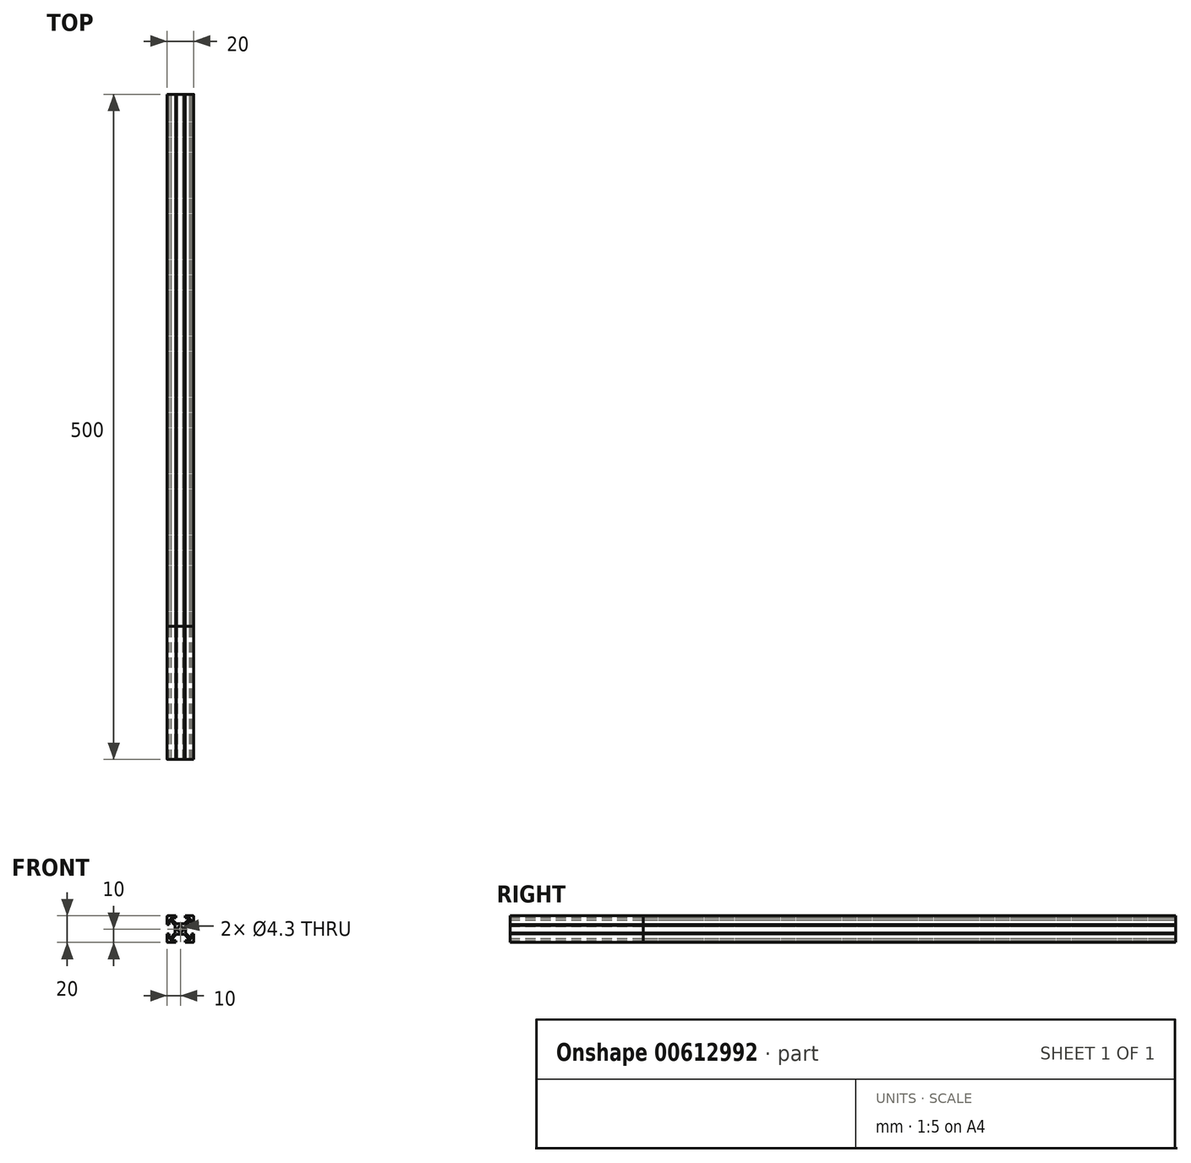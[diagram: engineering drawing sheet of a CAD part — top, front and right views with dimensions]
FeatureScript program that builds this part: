
annotation { "Feature Type Name" : "Feature", "Feature Type Description" : "" }
export const myFeature = defineFeature(function(context is Context, id is Id, definition is map)
    precondition{}
    {
        {
            var Q0;
            Q0=qCreatedBy(makeId("Front.planeOp"),FACE);
            var sketch = newSketch(context, id + "F0", { "sketchPlane" : qUnion([Q0])});
            skLineSegment(sketch, "E0", {"start": v(23.23, 0) * mm, "end": v(-24.5, 0) * mm, "construction": true});
            skLineSegment(sketch, "E1", {"start": v(0, 19.26) * mm, "end": v(0, -20.24) * mm, "construction": true});
            skLineSegment(sketch, "E2.bottom", {"start": v(4, 4) * mm, "end": v(-4, 4) * mm});
            skLineSegment(sketch, "E2.top", {"start": v(4, -4) * mm, "end": v(-4, -4) * mm});
            skLineSegment(sketch, "E2.left", {"start": v(4, 4) * mm, "end": v(4, -4) * mm});
            skLineSegment(sketch, "E2.right", {"start": v(-4, 4) * mm, "end": v(-4, -4) * mm});
            skPoint(sketch, "E2.middle", {"position": v(0, 0) * mm});
            skCircle(sketch, "E3", {"center": v(0, 0) * mm, "radius": 2.15 * mm});
            skLineSegment(sketch, "E4.right", {"start": v(10, 10) * mm, "end": v(10, -10) * mm, "construction": true});
            skLineSegment(sketch, "E5", {"start": v(-3.5, 10) * mm, "end": v(-9.67, 10) * mm});
            skLineSegment(sketch, "E6", {"start": v(-10, 9.67) * mm, "end": v(-10, 3.5) * mm});
            skLineSegment(sketch, "E7", {"start": v(-10, 3.5) * mm, "end": v(-8.5, 3.5) * mm});
            skLineSegment(sketch, "E8", {"start": v(-8.5, 3.5) * mm, "end": v(-8.5, 6.65) * mm});
            skLineSegment(sketch, "E9", {"start": v(-10, 10) * mm, "end": v(-4, 4) * mm, "construction": true});
            skLineSegment(sketch, "E10.trimOffspring", {"start": v(0, 10) * mm, "end": v(10, 10) * mm, "construction": true});
            skLineSegment(sketch, "E11", {"start": v(-3.5, 10) * mm, "end": v(-3.5, 8.5) * mm});
            skLineSegment(sketch, "E12", {"start": v(-3.5, 8.5) * mm, "end": v(-6.65, 8.5) * mm});
            skLineSegment(sketch, "E13", {"start": v(-6.88, 7.94) * mm, "end": v(-2.94, 4) * mm});
            skLineSegment(sketch, "E14", {"start": v(-4, 2.94) * mm, "end": v(-7.94, 6.88) * mm});
            skPoint(sketch, "E15.visualSharp", {"position": v(-7.44, 8.5) * mm});
            skArc(sketch, "E15.filletArc", {"start": v(-6.65, 8.5) * mm, "mid": v(-6.95, 8.3) * mm, "end": v(-6.88, 7.94) * mm});
            skPoint(sketch, "E16.visualSharp", {"position": v(-8.5, 7.44) * mm});
            skArc(sketch, "E16.filletArc", {"start": v(-7.94, 6.88) * mm, "mid": v(-8.3, 6.95) * mm, "end": v(-8.5, 6.65) * mm});
            skPoint(sketch, "E17.visualSharp", {"position": v(-10, 10) * mm});
            skArc(sketch, "E17.filletArc", {"start": v(-9.67, 10) * mm, "mid": v(-9.9, 9.9) * mm, "end": v(-10, 9.67) * mm});
            skLineSegment(sketch, "E18.MirrorCS", {"start": v(-10, -3.5) * mm, "end": v(-8.5, -3.5) * mm});
            skLineSegment(sketch, "E19.MirrorCS", {"start": v(-8.5, -3.5) * mm, "end": v(-8.5, -6.65) * mm});
            skLineSegment(sketch, "E20.MirrorCS", {"start": v(-10, -9.67) * mm, "end": v(-10, -3.5) * mm});
            skArc(sketch, "E21.MirrorCS", {"start": v(-9.67, -10) * mm, "mid": v(-9.9, -9.9) * mm, "end": v(-10, -9.67) * mm});
            skLineSegment(sketch, "E22.MirrorCS", {"start": v(-3.5, -10) * mm, "end": v(-9.67, -10) * mm});
            skLineSegment(sketch, "E23.MirrorCS", {"start": v(-3.5, -10) * mm, "end": v(-3.5, -8.5) * mm});
            skLineSegment(sketch, "E24.MirrorCS", {"start": v(-3.5, -8.5) * mm, "end": v(-6.65, -8.5) * mm});
            skArc(sketch, "E25.MirrorCS", {"start": v(-6.65, -8.5) * mm, "mid": v(-6.95, -8.3) * mm, "end": v(-6.88, -7.94) * mm});
            skLineSegment(sketch, "E26.MirrorCS", {"start": v(-6.88, -7.94) * mm, "end": v(-2.94, -4) * mm});
            skLineSegment(sketch, "E27.MirrorCS", {"start": v(-4, -2.94) * mm, "end": v(-7.94, -6.88) * mm});
            skArc(sketch, "E28.MirrorCS", {"start": v(-7.94, -6.88) * mm, "mid": v(-8.3, -6.95) * mm, "end": v(-8.5, -6.65) * mm});
            skLineSegment(sketch, "E29.MirrorCS", {"start": v(3.5, 10) * mm, "end": v(3.5, 8.5) * mm});
            skLineSegment(sketch, "E30.MirrorCS", {"start": v(3.5, 10) * mm, "end": v(9.67, 10) * mm});
            skLineSegment(sketch, "E31.MirrorCS", {"start": v(10, 9.67) * mm, "end": v(10, 3.5) * mm});
            skLineSegment(sketch, "E32.MirrorCS", {"start": v(8.5, 3.5) * mm, "end": v(8.5, 6.65) * mm});
            skLineSegment(sketch, "E33.MirrorCS", {"start": v(10, 3.5) * mm, "end": v(8.5, 3.5) * mm});
            skLineSegment(sketch, "E34.MirrorCS", {"start": v(4, 2.94) * mm, "end": v(7.94, 6.88) * mm});
            skLineSegment(sketch, "E35.MirrorCS", {"start": v(6.88, 7.94) * mm, "end": v(2.94, 4) * mm});
            skArc(sketch, "E36.MirrorCS", {"start": v(7.94, 6.88) * mm, "mid": v(8.3, 6.95) * mm, "end": v(8.5, 6.65) * mm});
            skArc(sketch, "E37.MirrorCS", {"start": v(6.65, 8.5) * mm, "mid": v(6.95, 8.3) * mm, "end": v(6.88, 7.94) * mm});
            skArc(sketch, "E38.MirrorCS", {"start": v(9.67, 10) * mm, "mid": v(9.9, 9.9) * mm, "end": v(10, 9.67) * mm});
            skLineSegment(sketch, "E39.MirrorCS", {"start": v(3.5, 8.5) * mm, "end": v(6.65, 8.5) * mm});
            skLineSegment(sketch, "E40.MirrorCS", {"start": v(4, -2.94) * mm, "end": v(7.94, -6.88) * mm});
            skLineSegment(sketch, "E41.MirrorCS", {"start": v(6.88, -7.94) * mm, "end": v(2.94, -4) * mm});
            skArc(sketch, "E42.MirrorCS", {"start": v(6.65, -8.5) * mm, "mid": v(6.95, -8.3) * mm, "end": v(6.88, -7.94) * mm});
            skArc(sketch, "E43.MirrorCS", {"start": v(7.94, -6.88) * mm, "mid": v(8.3, -6.95) * mm, "end": v(8.5, -6.65) * mm});
            skLineSegment(sketch, "E44.MirrorCS", {"start": v(8.5, -3.5) * mm, "end": v(8.5, -6.65) * mm});
            skLineSegment(sketch, "E45.MirrorCS", {"start": v(10, -3.5) * mm, "end": v(8.5, -3.5) * mm});
            skLineSegment(sketch, "E46.MirrorCS", {"start": v(10, 0) * mm, "end": v(10, -10) * mm, "construction": true});
            skArc(sketch, "E47.MirrorCS", {"start": v(9.67, -10) * mm, "mid": v(9.9, -9.9) * mm, "end": v(10, -9.67) * mm});
            skLineSegment(sketch, "E48.MirrorCS", {"start": v(3.5, -10) * mm, "end": v(3.5, -8.5) * mm});
            skLineSegment(sketch, "E49.MirrorCS", {"start": v(3.5, -8.5) * mm, "end": v(6.65, -8.5) * mm});
            skLineSegment(sketch, "E50.MirrorCS", {"start": v(10, -9.67) * mm, "end": v(10, -3.5) * mm});
            skLineSegment(sketch, "E51.MirrorCS", {"start": v(3.5, -10) * mm, "end": v(9.67, -10) * mm});
            skSolve(sketch);
        }
        {
            var Q0;
            Q0 = qSketchRegion(id + "F0", true);
            extrude(context, id + "F1", {"entities" : qUnion([Q0]), "depth" : 400 * mm, "offsetDistance" : 25 * mm});
        }
        {
            var Q0;
            Q0 = qSketchRegion(id + "F0", true);
            extrude(context, id + "F2", {"entities" : qUnion([Q0]), "depth" : 500 * mm, "offsetDistance" : 25 * mm});
        }
    });
